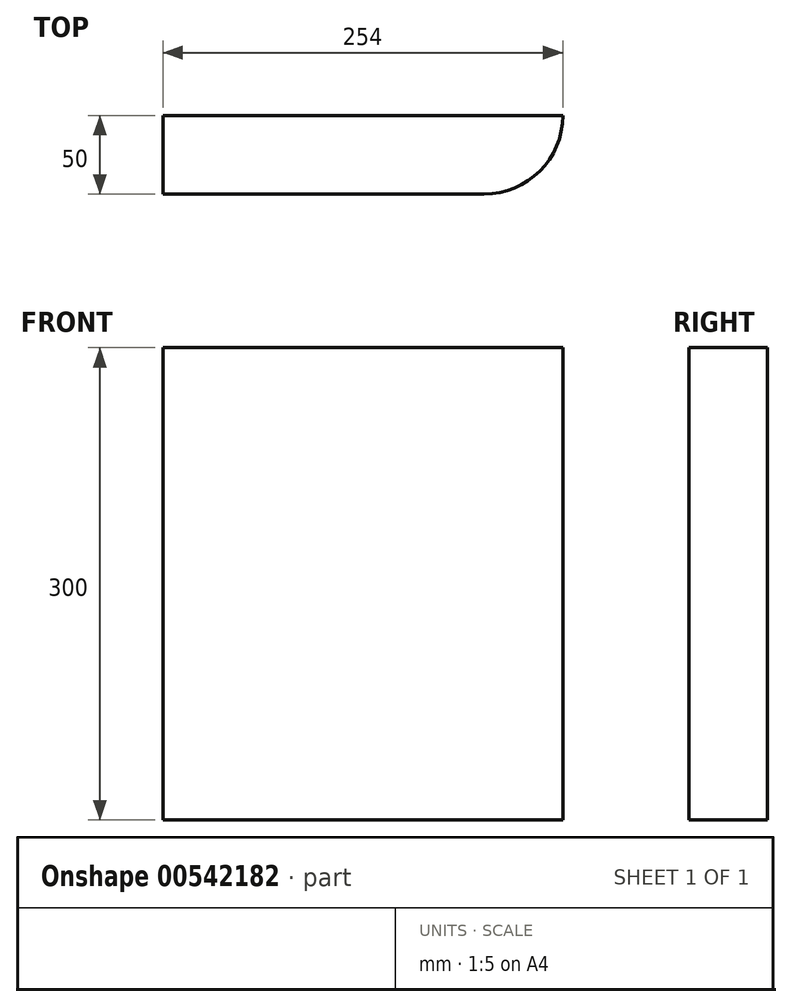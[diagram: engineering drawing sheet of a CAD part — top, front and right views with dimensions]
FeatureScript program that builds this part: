
annotation { "Feature Type Name" : "Feature", "Feature Type Description" : "" }
export const myFeature = defineFeature(function(context is Context, id is Id, definition is map)
    precondition{}
    {
        {
            var Q0;
            Q0=qCreatedBy(makeId("Front.planeOp"),FACE);
            var sketch = newSketch(context, id + "F0", { "sketchPlane" : qUnion([Q0])});
            skLineSegment(sketch, "E0.bottom", {"start": v(-127, 150) * mm, "end": v(127, 150) * mm});
            skLineSegment(sketch, "E0.top", {"start": v(-127, -150) * mm, "end": v(127, -150) * mm});
            skLineSegment(sketch, "E0.left", {"start": v(-127, 150) * mm, "end": v(-127, -150) * mm});
            skLineSegment(sketch, "E0.right", {"start": v(127, 150) * mm, "end": v(127, -150) * mm});
            skSolve(sketch);
        }
        {
            assignVariable(context, id + "F1", {"name" : "w", "anyValue" : 50});
        }
        {
            var Q0;
            Q0=makeQuery(id+"F0.imprint","IMPRINT",FACE,{"disambiguationData":[TD([[makeQuery(id+"F0.imprint","IMPRINT",EDGE,{"derivedFrom":sQuery(id+"F0.wireOp",EDGE,"E0.bottom")}),-1.0]])]});
            extrude(context, id + "F2", {"entities" : qUnion([Q0]), "depth" : (getVariable(context, 'w')) * mm, "offsetDistance" : 25 * mm});
        }
        {
            var Q0;
            Q0=makeQuery(id+"F2.opExtrude","CAP_EDGE",EDGE,{"disambiguationData":[OSD([sQuery(id+"F0.wireOp",EDGE,"E0.right")])],"isStart":false});
            fillet(context, id + "F3", {"entities" : qUnion([Q0]), "radius" : (getVariable(context, 'w')) * mm, "tangentPropagation" : true, "allowEdgeOverflow" : false});
        }
    });
